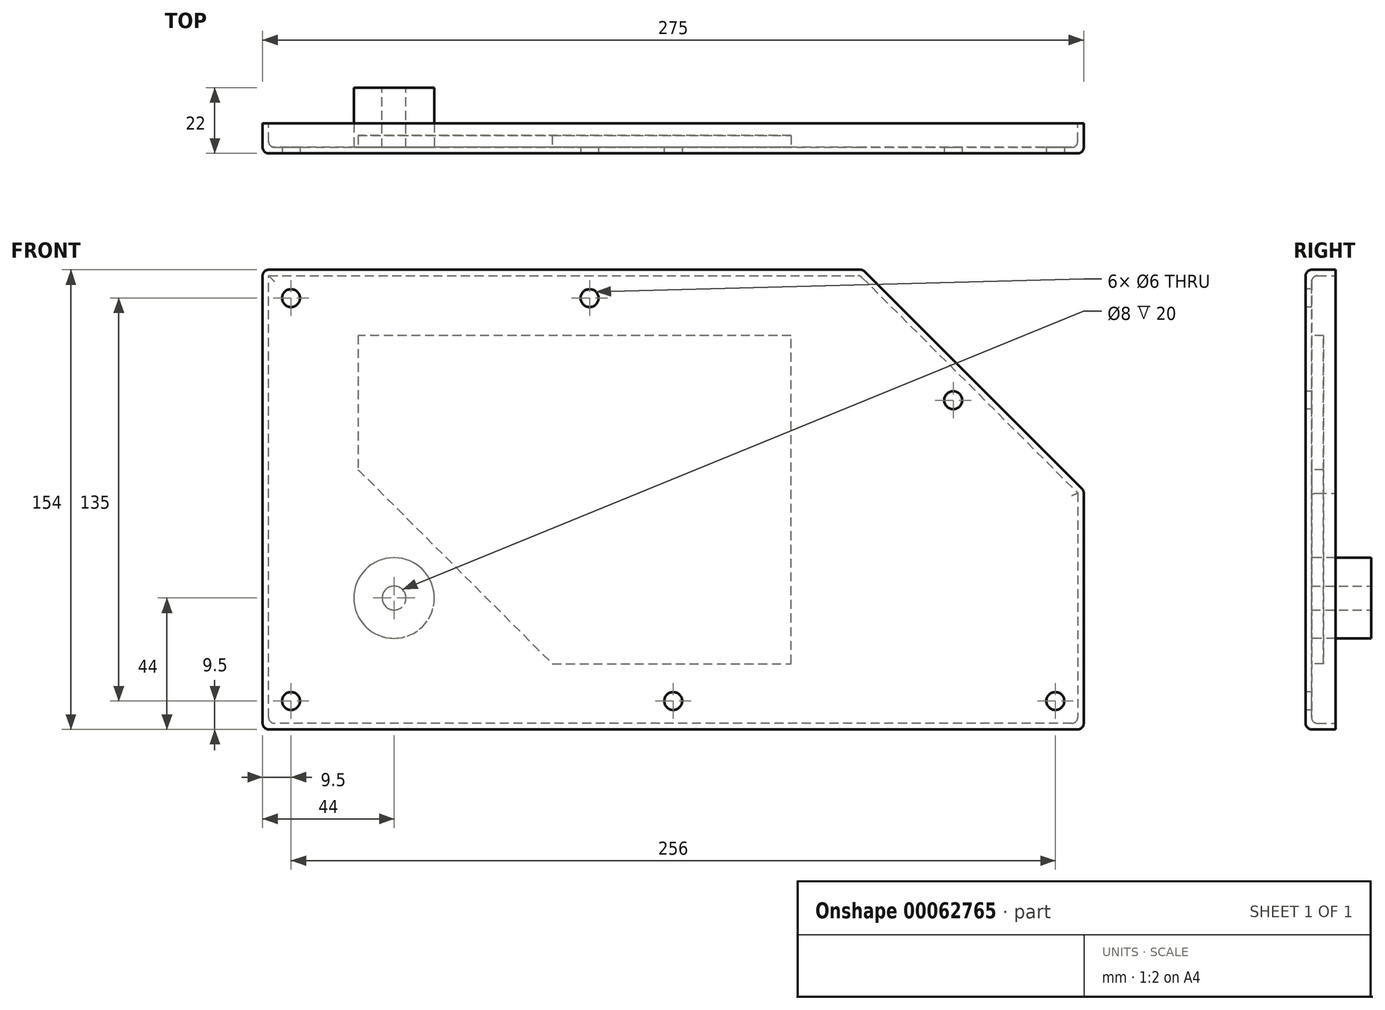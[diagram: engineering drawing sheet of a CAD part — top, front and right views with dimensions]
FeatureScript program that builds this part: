
annotation { "Feature Type Name" : "Feature", "Feature Type Description" : "" }
export const myFeature = defineFeature(function(context is Context, id is Id, definition is map)
    precondition{}
    {
        {
            var Q0;
            Q0=qCreatedBy(makeId("Front.planeOp"),FACE);
            var sketch = newSketch(context, id + "F0", { "sketchPlane" : qUnion([Q0])});
            skLineSegment(sketch, "E0", {"start": v(0, 0) * mm, "end": v(0, 154) * mm});
            skLineSegment(sketch, "E1", {"start": v(0, 154) * mm, "end": v(201, 154) * mm});
            skLineSegment(sketch, "E2", {"start": v(201, 154) * mm, "end": v(275, 80) * mm});
            skLineSegment(sketch, "E3", {"start": v(275, 80) * mm, "end": v(275, 0) * mm});
            skLineSegment(sketch, "E4", {"start": v(275, 0) * mm, "end": v(0, 0) * mm});
            skSolve(sketch);
        }
        {
            var Q0;
            Q0=makeQuery(id+"F0.imprint","IMPRINT",FACE,{"disambiguationData":[TD([[makeQuery(id+"F0.imprint","IMPRINT",EDGE,{"derivedFrom":sQuery(id+"F0.wireOp",EDGE,"E0")}),-1.0]])]});
            extrude(context, id + "F1", {"entities" : qUnion([Q0]), "depth" : 10 * mm});
        }
        {
            var Q0;
            Q0=makeQuery(id+"F1.opExtrude","CAP_FACE",FACE,{"disambiguationData":[OSD([sQuery(id+"F0.wireOp",EDGE,"E0"),sQuery(id+"F0.wireOp",EDGE,"E1"),sQuery(id+"F0.wireOp",EDGE,"E2"),sQuery(id+"F0.wireOp",EDGE,"E3"),sQuery(id+"F0.wireOp",EDGE,"E4")])],"isStart":true});
            shell(context, id + "F2", {"entities" : qUnion([Q0]), "thickness" : 2 * mm});
        }
        {
            var Q0;
            Q0=makeQuery(id+"F2.opShell","OFFSET_FACE",FACE,{"disambiguationData":[OSD([sQuery(id+"F0.wireOp",EDGE,"E0"),sQuery(id+"F0.wireOp",EDGE,"E1"),sQuery(id+"F0.wireOp",EDGE,"E2"),sQuery(id+"F0.wireOp",EDGE,"E3"),sQuery(id+"F0.wireOp",EDGE,"E4")])]});
            var sketch = newSketch(context, id + "F3", { "sketchPlane" : qUnion([Q0])});
            skCircle(sketch, "E5", {"center": v(-67, 102) * mm, "radius": 22.5 * mm});
            skCircle(sketch, "E6", {"center": v(-137.5, 52) * mm, "radius": 22.5 * mm});
            skSolve(sketch);
        }
        {
            var Q0;
            Q0=makeQuery(id+"F2.opShell","OFFSET_FACE",FACE,{"disambiguationData":[OSD([sQuery(id+"F0.wireOp",EDGE,"E0"),sQuery(id+"F0.wireOp",EDGE,"E1"),sQuery(id+"F0.wireOp",EDGE,"E2"),sQuery(id+"F0.wireOp",EDGE,"E3"),sQuery(id+"F0.wireOp",EDGE,"E4")])]});
            var sketch = newSketch(context, id + "F4", { "sketchPlane" : qUnion([Q0])});
            skLineSegment(sketch, "E7", {"start": v(-32, 132) * mm, "end": v(-32, 87) * mm});
            skLineSegment(sketch, "E8", {"start": v(-32, 87) * mm, "end": v(-97, 22) * mm});
            skLineSegment(sketch, "E9", {"start": v(-97, 22) * mm, "end": v(-177, 22) * mm});
            skLineSegment(sketch, "E10", {"start": v(-177, 22) * mm, "end": v(-177, 132) * mm});
            skLineSegment(sketch, "E11", {"start": v(-177, 132) * mm, "end": v(-32, 132) * mm});
            skSolve(sketch);
        }
        {
            var Q0;
            Q0=qSketchRegion(id+"F4",true);
            var Q1;
            Q1=makeQuery(id+"F4.imprint","IMPRINT",FACE,{"disambiguationData":[TD([[makeQuery(id+"F4.imprint","IMPRINT",EDGE,{"derivedFrom":sQuery(id+"F4.wireOp",EDGE,"E7")}),-1.0]])]});
            extrude(context, id + "F5", {"entities" : qUnion([Q0, Q1]), "operationType" : NewBodyOperationType.ADD, "depth" : 4 * mm});
        }
        {
            var Q0;
            Q0=makeQuery(id+"F2.opShell","OFFSET_FACE",FACE,{"disambiguationData":[OSD([sQuery(id+"F0.wireOp",EDGE,"E0"),sQuery(id+"F0.wireOp",EDGE,"E1"),sQuery(id+"F0.wireOp",EDGE,"E2"),sQuery(id+"F0.wireOp",EDGE,"E3"),sQuery(id+"F0.wireOp",EDGE,"E4")])]});
            var sketch = newSketch(context, id + "F6", { "sketchPlane" : qUnion([Q0])});
            skCircle(sketch, "E12", {"center": v(-44, 44) * mm, "radius": 13.5 * mm});
            skSolve(sketch);
        }
        {
            var Q0;
            Q0=qSketchRegion(id+"F6",true);
            extrude(context, id + "F7", {"entities" : qUnion([Q0]), "operationType" : NewBodyOperationType.ADD, "depth" : 20 * mm});
        }
        {
            var Q0;
            Q0=makeQuery(id+"F7.opExtrude","CAP_FACE",FACE,{"disambiguationData":[OSD([sQuery(id+"F6.wireOp",EDGE,"E12")])],"isStart":false});
            var sketch = newSketch(context, id + "F8", { "sketchPlane" : qUnion([Q0])});
            skPoint(sketch, "E13", {"position": v(-44, 44) * mm});
            skCircle(sketch, "E14", {"center": v(-44, 44) * mm, "radius": 4 * mm});
            skSolve(sketch);
        }
        {
            var Q0;
            Q0=makeQuery(id+"F8.imprint","IMPRINT",FACE,{"disambiguationData":[TD([[makeQuery(id+"F8.imprint","IMPRINT",EDGE,{"derivedFrom":sQuery(id+"F8.wireOp",EDGE,"E14")}),1.0]])]});
            var Q1;
            Q1=makeQuery(id+"F2.opShell","OFFSET_FACE",FACE,{"disambiguationData":[OSD([sQuery(id+"F0.wireOp",EDGE,"E0"),sQuery(id+"F0.wireOp",EDGE,"E1"),sQuery(id+"F0.wireOp",EDGE,"E2"),sQuery(id+"F0.wireOp",EDGE,"E3"),sQuery(id+"F0.wireOp",EDGE,"E4")])]});
            extrude(context, id + "F9", {"entities" : qUnion([Q0]), "operationType" : NewBodyOperationType.REMOVE, "endBound" : BoundingType.UP_TO_SURFACE, "oppositeDirection" : true, "endBoundEntityFace" : qUnion([Q1]), "depth" : 25 * mm});
        }
        {
            var Q0;
            Q0=makeQuery(id+"F1.opExtrude","CAP_FACE",FACE,{"disambiguationData":[OSD([sQuery(id+"F0.wireOp",EDGE,"E0"),sQuery(id+"F0.wireOp",EDGE,"E1"),sQuery(id+"F0.wireOp",EDGE,"E2"),sQuery(id+"F0.wireOp",EDGE,"E3"),sQuery(id+"F0.wireOp",EDGE,"E4")])],"isStart":false});
            var sketch = newSketch(context, id + "F10", { "sketchPlane" : qUnion([Q0])});
            skLineSegment(sketch, "E15.0", {"start": v(9.5, 9.5) * mm, "end": v(265.5, 9.5) * mm, "construction": true});
            skLineSegment(sketch, "E15.1", {"start": v(9.5, 144.5) * mm, "end": v(9.5, 9.5) * mm, "construction": true});
            skLineSegment(sketch, "E15.2", {"start": v(265.5, 9.5) * mm, "end": v(265.5, 76.06) * mm, "construction": true});
            skLineSegment(sketch, "E15.3", {"start": v(265.5, 76.06) * mm, "end": v(197.06, 144.5) * mm, "construction": true});
            skLineSegment(sketch, "E15.4", {"start": v(197.06, 144.5) * mm, "end": v(9.5, 144.5) * mm, "construction": true});
            skPoint(sketch, "E16", {"position": v(9.5, 144.5) * mm});
            skPoint(sketch, "E17", {"position": v(109.5, 144.5) * mm});
            skPoint(sketch, "E18", {"position": v(231.28, 110.28) * mm});
            skPoint(sketch, "E19", {"position": v(265.5, 9.5) * mm});
            skPoint(sketch, "E20", {"position": v(137.5, 9.5) * mm});
            skPoint(sketch, "E21", {"position": v(9.5, 9.5) * mm});
            skSolve(sketch);
        }
        {
            var Q0;
            Q0=sQuery(id+"F10.wireOp",VERTEX,"E16");
            var Q1;
            Q1=sQuery(id+"F10.wireOp",VERTEX,"E17");
            var Q2;
            Q2=sQuery(id+"F10.wireOp",VERTEX,"E18");
            var Q3;
            Q3=sQuery(id+"F10.wireOp",VERTEX,"E19");
            var Q4;
            Q4=sQuery(id+"F10.wireOp",VERTEX,"E20");
            var Q5;
            Q5=sQuery(id+"F10.wireOp",VERTEX,"E21");
            var Q6;
            Q6=makeQuery(id+"F1.opExtrude","SWEPT_BODY",BODY,{"disambiguationData":[OSD([sQuery(id+"F0.wireOp",EDGE,"E0"),sQuery(id+"F0.wireOp",EDGE,"E1"),sQuery(id+"F0.wireOp",EDGE,"E2"),sQuery(id+"F0.wireOp",EDGE,"E3"),sQuery(id+"F0.wireOp",EDGE,"E4")])]});
            hole(context, id + "F11", {"style" : HoleStyle.SIMPLE, "holeDiameter" : 6 * mm, "endStyle" : HoleEndStyle.THROUGH, "locations" : qUnion([Q0, Q1, Q2, Q3, Q4, Q5]), "scope" : qUnion([Q6])});
        }
        {
            var Q0;
            Q0=makeQuery(id+"F1.opExtrude","CAP_EDGE",EDGE,{"disambiguationData":[OSD([sQuery(id+"F0.wireOp",EDGE,"E0")])],"isStart":false});
            var Q1;
            Q1=makeQuery(id+"F1.opExtrude","CAP_EDGE",EDGE,{"disambiguationData":[OSD([sQuery(id+"F0.wireOp",EDGE,"E4")])],"isStart":false});
            var Q2;
            Q2=makeQuery(id+"F1.opExtrude","CAP_EDGE",EDGE,{"disambiguationData":[OSD([sQuery(id+"F0.wireOp",EDGE,"E2")])],"isStart":false});
            var Q3;
            Q3=makeQuery(id+"F1.opExtrude","CAP_EDGE",EDGE,{"disambiguationData":[OSD([sQuery(id+"F0.wireOp",EDGE,"E3")])],"isStart":false});
            var Q4;
            Q4=makeQuery(id+"F1.opExtrude","SWEPT_EDGE",EDGE,{"disambiguationData":[OSD([sQuery(id+"F0.wireOp",EDGE,"E3"),sQuery(id+"F0.wireOp",EDGE,"E4")])]});
            var Q5;
            Q5=makeQuery(id+"F1.opExtrude","SWEPT_EDGE",EDGE,{"disambiguationData":[OSD([sQuery(id+"F0.wireOp",EDGE,"E2"),sQuery(id+"F0.wireOp",EDGE,"E3")])]});
            var Q6;
            Q6=makeQuery(id+"F1.opExtrude","SWEPT_EDGE",EDGE,{"disambiguationData":[OSD([sQuery(id+"F0.wireOp",EDGE,"E1"),sQuery(id+"F0.wireOp",EDGE,"E2")])]});
            var Q7;
            Q7=makeQuery(id+"F1.opExtrude","SWEPT_EDGE",EDGE,{"disambiguationData":[OSD([sQuery(id+"F0.wireOp",EDGE,"E0"),sQuery(id+"F0.wireOp",EDGE,"E4")])]});
            var Q8;
            Q8=makeQuery(id+"F1.opExtrude","CAP_EDGE",EDGE,{"disambiguationData":[OSD([sQuery(id+"F0.wireOp",EDGE,"E1")])],"isStart":false});
            var Q9;
            Q9=makeQuery(id+"F1.opExtrude","SWEPT_EDGE",EDGE,{"disambiguationData":[OSD([sQuery(id+"F0.wireOp",EDGE,"E0"),sQuery(id+"F0.wireOp",EDGE,"E1")])]});
            fillet(context, id + "F12", {"entities" : qUnion([Q0, Q1, Q2, Q3, Q4, Q5, Q6, Q7, Q8, Q9]), "radius" : 2 * mm, "tangentPropagation" : true, "allowEdgeOverflow" : false});
        }
        {
            var Q0;
            Q0=makeQuery(id+"F2.opShell","OFFSET_EDGE",EDGE,{"disambiguationData":[OSD([sQuery(id+"F0.wireOp",EDGE,"E3"),sQuery(id+"F0.wireOp",EDGE,"E4")])]});
            var Q1;
            {var subQ0=sQuery(id+"F0.wireOp",EDGE,"E4");Q1=makeQuery(id+"F2.opShell","OFFSET_EDGE",EDGE,{"disambiguationData":[OSD([subQ0]),TDD([makeQuery(id+"F1.opExtrude","CAP_EDGE",EDGE,{"disambiguationData":[OSD([subQ0])],"isStart":false})])]});}
            var Q2;
            {var subQ0=sQuery(id+"F0.wireOp",EDGE,"E3");Q2=makeQuery(id+"F2.opShell","OFFSET_EDGE",EDGE,{"disambiguationData":[OSD([subQ0]),TDD([makeQuery(id+"F1.opExtrude","CAP_EDGE",EDGE,{"disambiguationData":[OSD([subQ0])],"isStart":false})])]});}
            var Q3;
            {var subQ0=sQuery(id+"F0.wireOp",EDGE,"E2");Q3=makeQuery(id+"F2.opShell","OFFSET_EDGE",EDGE,{"disambiguationData":[OSD([subQ0]),TDD([makeQuery(id+"F1.opExtrude","CAP_EDGE",EDGE,{"disambiguationData":[OSD([subQ0])],"isStart":false})])]});}
            var Q4;
            Q4=makeQuery(id+"F2.opShell","OFFSET_EDGE",EDGE,{"disambiguationData":[OSD([sQuery(id+"F0.wireOp",EDGE,"E1"),sQuery(id+"F0.wireOp",EDGE,"E2")])]});
            var Q5;
            {var subQ0=sQuery(id+"F0.wireOp",EDGE,"E1");Q5=makeQuery(id+"F2.opShell","OFFSET_EDGE",EDGE,{"disambiguationData":[OSD([subQ0]),TDD([makeQuery(id+"F1.opExtrude","CAP_EDGE",EDGE,{"disambiguationData":[OSD([subQ0])],"isStart":false})])]});}
            var Q6;
            Q6=makeQuery(id+"F2.opShell","OFFSET_EDGE",EDGE,{"disambiguationData":[OSD([sQuery(id+"F0.wireOp",EDGE,"E0"),sQuery(id+"F0.wireOp",EDGE,"E4")])]});
            var Q7;
            {var subQ0=sQuery(id+"F0.wireOp",EDGE,"E0");Q7=makeQuery(id+"F2.opShell","OFFSET_EDGE",EDGE,{"disambiguationData":[OSD([subQ0]),TDD([makeQuery(id+"F1.opExtrude","CAP_EDGE",EDGE,{"disambiguationData":[OSD([subQ0])],"isStart":false})])]});}
            fillet(context, id + "F13", {"entities" : qUnion([Q0, Q1, Q2, Q3, Q4, Q5, Q6, Q7]), "radius" : 2 * mm, "tangentPropagation" : true, "allowEdgeOverflow" : false});
        }
    });
